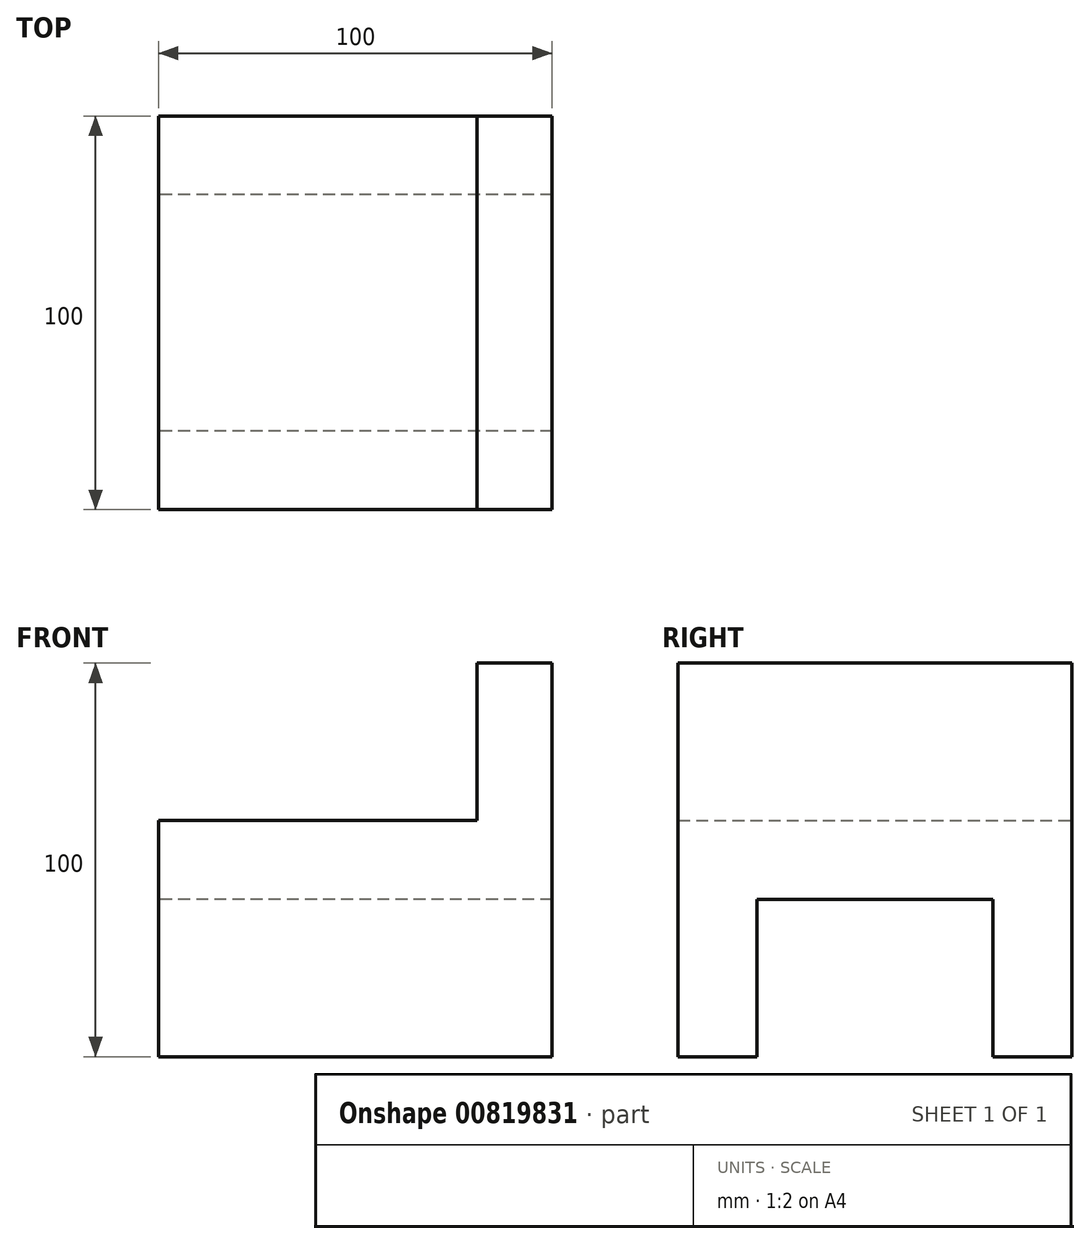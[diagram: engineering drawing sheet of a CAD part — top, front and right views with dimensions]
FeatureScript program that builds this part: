
annotation { "Feature Type Name" : "Feature", "Feature Type Description" : "" }
export const myFeature = defineFeature(function(context is Context, id is Id, definition is map)
    precondition{}
    {
        {
            var Q0;
            Q0=qCreatedBy(makeId("Top.planeOp"),FACE);
            var sketch = newSketch(context, id + "F0", { "sketchPlane" : qUnion([Q0])});
            skLineSegment(sketch, "E0.bottom", {"start": v(-50, -50) * mm, "end": v(50, -50) * mm});
            skLineSegment(sketch, "E0.top", {"start": v(-50, 50) * mm, "end": v(50, 50) * mm});
            skLineSegment(sketch, "E0.left", {"start": v(-50, -50) * mm, "end": v(-50, 50) * mm});
            skLineSegment(sketch, "E0.right", {"start": v(50, -50) * mm, "end": v(50, 50) * mm});
            skPoint(sketch, "E0.middle", {"position": v(0, 0) * mm});
            skSolve(sketch);
        }
        {
            var Q0;
            Q0 = qSketchRegion(id + "F0", true);
            extrude(context, id + "F1", {"entities" : qUnion([Q0]), "depth" : 100 * mm, "offsetDistance" : 25 * mm});
        }
        {
            var Q0;
            Q0=makeQuery(id+"F1.opExtrude","CAP_FACE",FACE,{"disambiguationData":[OSD([sQuery(id+"F0.wireOp",EDGE,"E0.bottom"),sQuery(id+"F0.wireOp",EDGE,"E0.top"),sQuery(id+"F0.wireOp",EDGE,"E0.left"),sQuery(id+"F0.wireOp",EDGE,"E0.right")])],"isStart":false});
            var sketch = newSketch(context, id + "F2", { "sketchPlane" : qUnion([Q0])});
            skLineSegment(sketch, "E1.bottom", {"start": v(-50, 50) * mm, "end": v(30.88, 50) * mm});
            skLineSegment(sketch, "E1.top", {"start": v(-50, -50) * mm, "end": v(30.88, -50) * mm});
            skLineSegment(sketch, "E1.left", {"start": v(-50, 50) * mm, "end": v(-50, -50) * mm});
            skLineSegment(sketch, "E1.right", {"start": v(30.88, 50) * mm, "end": v(30.88, -50) * mm});
            skSolve(sketch);
        }
        {
            var Q0;
            Q0=makeQuery(id+"F2.imprint","IMPRINT",FACE,{"disambiguationData":[TD([[makeQuery(id+"F2.imprint","IMPRINT",EDGE,{"derivedFrom":sQuery(id+"F2.wireOp",EDGE,"E1.bottom")}),-1.0]])]});
            extrude(context, id + "F3", {"entities" : qUnion([Q0]), "operationType" : NewBodyOperationType.REMOVE, "oppositeDirection" : true, "depth" : 40 * mm, "offsetDistance" : 25 * mm});
        }
        {
            var Q0;
            Q0=makeQuery(id+"F1.opExtrude","SWEPT_FACE",FACE,{"disambiguationData":[OSD([sQuery(id+"F0.wireOp",EDGE,"E0.left")])]});
            var sketch = newSketch(context, id + "F4", { "sketchPlane" : qUnion([Q0])});
            skLineSegment(sketch, "E2.bottom", {"start": v(-30, 0) * mm, "end": v(30, 0) * mm});
            skLineSegment(sketch, "E2.top", {"start": v(-30, 40) * mm, "end": v(30, 40) * mm});
            skLineSegment(sketch, "E2.left", {"start": v(-30, 0) * mm, "end": v(-30, 40) * mm});
            skLineSegment(sketch, "E2.right", {"start": v(30, 0) * mm, "end": v(30, 40) * mm});
            skSolve(sketch);
        }
        {
            var Q0;
            Q0 = qSketchRegion(id + "F4", true);
            extrude(context, id + "F5", {"entities" : qUnion([Q0]), "operationType" : NewBodyOperationType.REMOVE, "endBound" : BoundingType.THROUGH_ALL, "oppositeDirection" : true, "depth" : 25 * mm, "offsetDistance" : 25 * mm});
        }
    });
